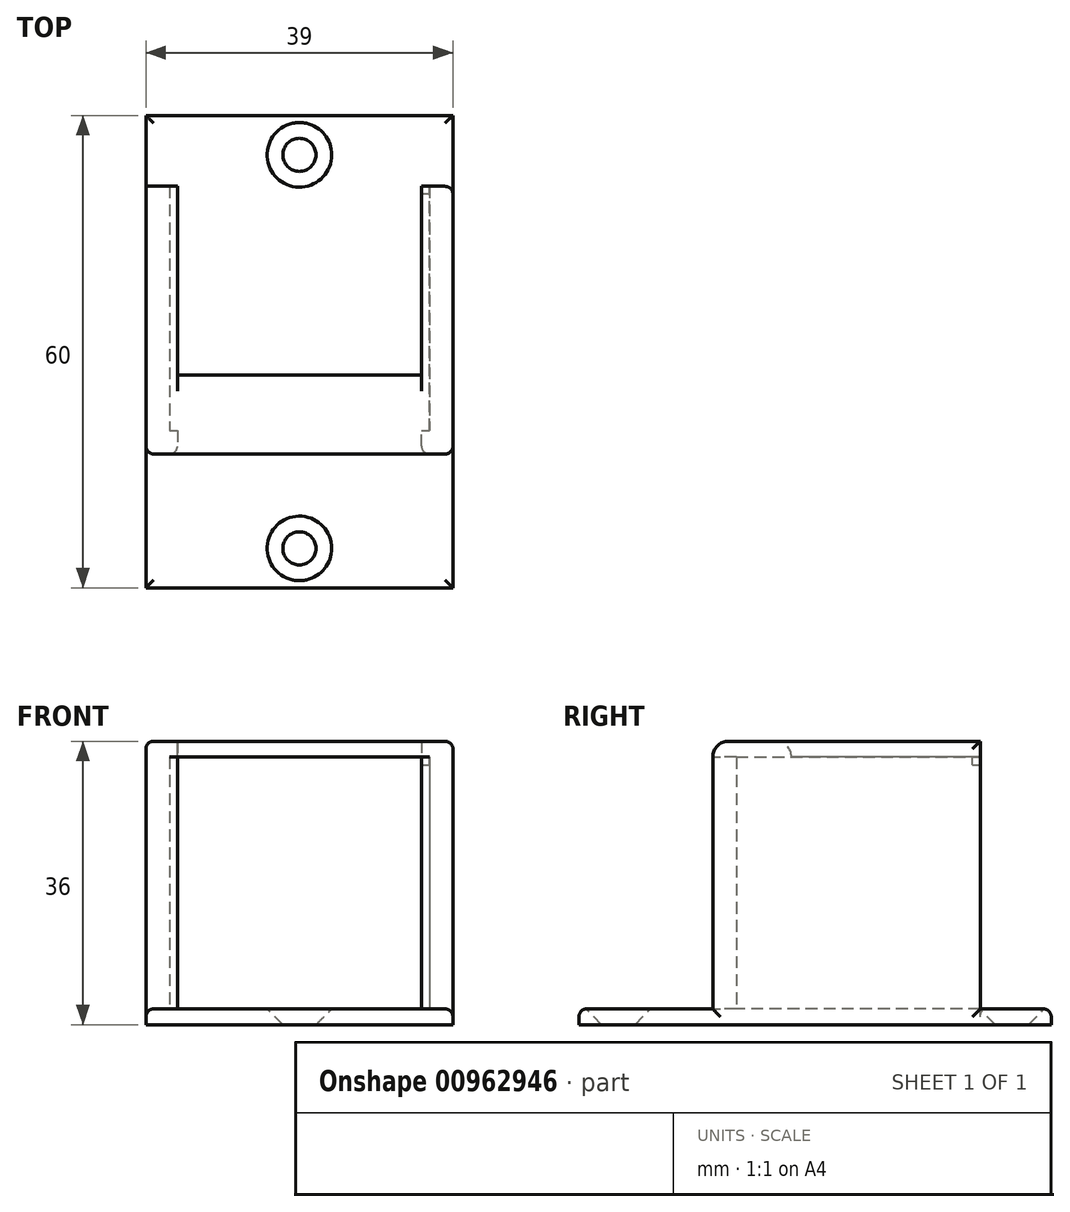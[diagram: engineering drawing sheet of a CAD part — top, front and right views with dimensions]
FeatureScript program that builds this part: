
annotation { "Feature Type Name" : "Feature", "Feature Type Description" : "" }
export const myFeature = defineFeature(function(context is Context, id is Id, definition is map)
    precondition{}
    {
        {
            var Q0;
            Q0=qCreatedBy(makeId("Top.planeOp"),FACE);
            var sketch = newSketch(context, id + "F0", { "sketchPlane" : qUnion([Q0])});
            skLineSegment(sketch, "E0.bottom", {"start": v(19.5, 25) * mm, "end": v(16.5, 25) * mm});
            skLineSegment(sketch, "E0.top", {"start": v(19.5, -25) * mm, "end": v(-19.5, -25) * mm});
            skLineSegment(sketch, "E0.left", {"start": v(19.5, 25) * mm, "end": v(19.5, -25) * mm});
            skLineSegment(sketch, "E0.right", {"start": v(-19.5, 25) * mm, "end": v(-19.5, -25) * mm});
            skPoint(sketch, "E1.middle", {"position": v(0, 0) * mm});
            skLineSegment(sketch, "E2", {"start": v(0, -25) * mm, "end": v(0, -20) * mm, "construction": true});
            skCircle(sketch, "E3", {"center": v(0, -20) * mm, "radius": 2.1 * mm});
            skLineSegment(sketch, "E4.bottom", {"start": v(-16.5, 15) * mm, "end": v(16.5, 15) * mm});
            skLineSegment(sketch, "E4.top", {"start": v(-16.5, -15) * mm, "end": v(16.5, -15) * mm});
            skLineSegment(sketch, "E4.left", {"start": v(-16.5, 15) * mm, "end": v(-16.5, -15) * mm});
            skLineSegment(sketch, "E4.right", {"start": v(16.5, 15) * mm, "end": v(16.5, -15) * mm});
            skLineSegment(sketch, "E5", {"start": v(-16.5, 15) * mm, "end": v(-16.5, 25) * mm});
            skLineSegment(sketch, "E6", {"start": v(-16.5, 25) * mm, "end": v(-16.5, -25) * mm});
            skLineSegment(sketch, "E7", {"start": v(16.5, -25) * mm, "end": v(16.5, 25) * mm});
            skLineSegment(sketch, "E8", {"start": v(-16.5, -15) * mm, "end": v(-19.5, -15) * mm});
            skLineSegment(sketch, "E9", {"start": v(16.5, -15) * mm, "end": v(19.5, -15) * mm});
            skLineSegment(sketch, "E10", {"start": v(16.5, -15) * mm, "end": v(15.5, -15) * mm});
            skLineSegment(sketch, "E11", {"start": v(16.5, -15) * mm, "end": v(16.5, -18) * mm, "construction": true});
            skLineSegment(sketch, "E12", {"start": v(16.5, -18) * mm, "end": v(19.5, -18) * mm});
            skLineSegment(sketch, "E13", {"start": v(-16.5, -18) * mm, "end": v(-19.5, -18) * mm});
            skLineSegment(sketch, "E14", {"start": v(-16.5, -15) * mm, "end": v(-15.5, -15) * mm});
            skLineSegment(sketch, "E15", {"start": v(-15.5, -15) * mm, "end": v(-15.5, -18) * mm});
            skLineSegment(sketch, "E16", {"start": v(-15.5, -18) * mm, "end": v(-16.5, -18) * mm});
            skLineSegment(sketch, "E17", {"start": v(16.5, -18) * mm, "end": v(15.5, -18) * mm});
            skLineSegment(sketch, "E18", {"start": v(15.5, -18) * mm, "end": v(15.5, -15) * mm});
            skLineSegment(sketch, "E19", {"start": v(-19.5, 15) * mm, "end": v(-19.5, 16) * mm});
            skLineSegment(sketch, "E20", {"start": v(-19.5, 16) * mm, "end": v(-16.5, 16) * mm});
            skLineSegment(sketch, "E21", {"start": v(-16.5, 16) * mm, "end": v(-16.5, 15) * mm});
            skLineSegment(sketch, "E22", {"start": v(16.5, 15) * mm, "end": v(16.5, 16) * mm});
            skLineSegment(sketch, "E23", {"start": v(16.5, 16) * mm, "end": v(19.5, 16) * mm});
            skLineSegment(sketch, "E24.trimOffspring", {"start": v(-16.5, 25) * mm, "end": v(-19.5, 25) * mm});
            skPoint(sketch, "E25.startSnap0", {"position": v(-18, 25) * mm});
            skLineSegment(sketch, "E26", {"start": v(-19.5, 25) * mm, "end": v(19.5, 25) * mm});
            skLineSegment(sketch, "E27", {"start": v(0, 25) * mm, "end": v(0, 20) * mm, "construction": true});
            skCircle(sketch, "E28", {"center": v(0, 20) * mm, "radius": 2.1 * mm});
            skLineSegment(sketch, "E29", {"start": v(19.5, -25) * mm, "end": v(19.5, -35) * mm});
            skLineSegment(sketch, "E30", {"start": v(19.5, -35) * mm, "end": v(-19.5, -35) * mm});
            skLineSegment(sketch, "E31", {"start": v(-19.5, -35) * mm, "end": v(-19.5, -25) * mm});
            skLineSegment(sketch, "E32", {"start": v(0, -35) * mm, "end": v(0, -30) * mm, "construction": true});
            skCircle(sketch, "E33", {"center": v(0, -30) * mm, "radius": 2.1 * mm});
            skSolve(sketch);
        }
        {
            var Q0;
            {var subQ1=sQuery(id+"F0.wireOp",EDGE,"E4.left");var subQ2=sQuery(id+"F0.wireOp",EDGE,"E4.bottom");var subQ3=sQuery(id+"F0.wireOp",EDGE,"E20");var subQ10=sQuery(id+"F0.wireOp",EDGE,"E0.bottom");var subQ14=sQuery(id+"F0.wireOp",EDGE,"E4.right");var subQ19=sQuery(id+"F0.wireOp",EDGE,"E8");var subQ21=makeQuery(id+"F0.imprint","IMPRINT",EDGE,{"derivedFrom":subQ19});var subQ22=makeQuery(id+"F0.imprint","IMPRINT",EDGE,{"derivedFrom":subQ3});var subQ23=sQuery(id+"F0.wireOp",EDGE,"E9");var subQ24=makeQuery(id+"F0.imprint","IMPRINT",EDGE,{"derivedFrom":subQ23});var subQ36=sQuery(id+"F0.wireOp",EDGE,"E29");var subQ39=sQuery(id+"F0.wireOp",EDGE,"E13");var subQ41=makeQuery(id+"F0.imprint","IMPRINT",EDGE,{"derivedFrom":subQ39});var subQ44=sQuery(id+"F0.wireOp",EDGE,"E12");var subQ47=makeQuery(id+"F0.imprint","IMPRINT",EDGE,{"derivedFrom":subQ44});Q0=qUnion([makeQuery(id+"F0.imprint","IMPRINT",FACE,{"disambiguationData":[TD([[makeQuery(id+"F0.imprint","IMPRINT",EDGE,{"derivedFrom":subQ10}),1.0]])]}),makeQuery(id+"F0.imprint","IMPRINT",FACE,{"disambiguationData":[TD([[subQ22,1.0]])]}),makeQuery(id+"F0.imprint","IMPRINT",FACE,{"disambiguationData":[TD([[subQ47,-1.0]])]}),makeQuery(id+"F0.imprint","IMPRINT",FACE,{"disambiguationData":[TD([[subQ41,1.0]])]}),makeQuery(id+"F0.imprint","IMPRINT",FACE,{"disambiguationData":[TD([[subQ24,-1.0]])]}),makeQuery(id+"F0.imprint","IMPRINT",FACE,{"disambiguationData":[TD([[subQ21,1.0]])]}),makeQuery(id+"F0.imprint","IMPRINT",FACE,{"disambiguationData":[TD([[makeQuery(id+"F0.imprint","IMPRINT",EDGE,{"derivedFrom":subQ36}),-1.0]])]}),makeQuery(id+"F0.imprint","IMPRINT",FACE,{"disambiguationData":[TD([[makeQuery(id+"F0.imprint","IMPRINT",EDGE,{"derivedFrom":subQ14}),1.0]])]}),makeQuery(id+"F0.imprint","IMPRINT",FACE,{"disambiguationData":[TD([[makeQuery(id+"F0.imprint","IMPRINT",EDGE,{"derivedFrom":subQ1}),-1.0]])]}),makeQuery(id+"F0.imprint","IMPRINT",FACE,{"disambiguationData":[TD([[makeQuery(id+"F0.imprint","IMPRINT",EDGE,{"derivedFrom":subQ2}),1.0]])]})]);}
            var Q1;
            Q1=makeQuery(id+"F0.imprint","IMPRINT",FACE,{"disambiguationData":[TD([[makeQuery(id+"F0.imprint","IMPRINT",EDGE,{"derivedFrom":sQuery(id+"F0.wireOp",EDGE,"E4.bottom")}),-1.0]])]});
            var Q2;
            {var subQ0=sQuery(id+"F0.wireOp",EDGE,"E15");Q2=makeQuery(id+"F0.imprint","IMPRINT",FACE,{"disambiguationData":[TD([[makeQuery(id+"F0.imprint","IMPRINT",EDGE,{"derivedFrom":subQ0}),-1.0]])]});}
            var Q3;
            {var subQ4=sQuery(id+"F0.wireOp",EDGE,"E17");Q3=makeQuery(id+"F0.imprint","IMPRINT",FACE,{"disambiguationData":[TD([[makeQuery(id+"F0.imprint","IMPRINT",EDGE,{"derivedFrom":subQ4}),-1.0]])]});}
            var Q4;
            Q4=makeQuery(id+"F0.imprint","IMPRINT",FACE,{"disambiguationData":[TD([[makeQuery(id+"F0.imprint","IMPRINT",EDGE,{"derivedFrom":sQuery(id+"F0.wireOp",EDGE,"E3")}),-1.0]])]});
            var Q5;
            Q5=makeQuery(id+"F0.imprint","IMPRINT",FACE,{"disambiguationData":[TD([[makeQuery(id+"F0.imprint","IMPRINT",EDGE,{"derivedFrom":sQuery(id+"F0.wireOp",EDGE,"E3")}),1.0]])]});
            extrude(context, id + "F1", {"entities" : qUnion([Q0, Q1, Q2, Q3, Q4, Q5]), "oppositeDirection" : true, "depth" : 2 * mm, "offsetDistance" : 25 * mm});
        }
        {
            var Q0;
            {var subQ1=sQuery(id+"F0.wireOp",EDGE,"E4.left");Q0=makeQuery(id+"F0.imprint","IMPRINT",FACE,{"disambiguationData":[TD([[makeQuery(id+"F0.imprint","IMPRINT",EDGE,{"derivedFrom":subQ1}),-1.0]])]});}
            var Q1;
            {var subQ0=sQuery(id+"F0.wireOp",EDGE,"E8");Q1=makeQuery(id+"F0.imprint","IMPRINT",FACE,{"disambiguationData":[TD([[makeQuery(id+"F0.imprint","IMPRINT",EDGE,{"derivedFrom":subQ0}),1.0]])]});}
            var Q2;
            {var subQ0=sQuery(id+"F0.wireOp",EDGE,"nsobvpxD-CgMy-OlzF-O2xX-1xosLkDLj3p1");Q2=makeQuery(id+"F0.imprint","IMPRINT",FACE,{"disambiguationData":[TD([[makeQuery(id+"F0.imprint","IMPRINT",EDGE,{"derivedFrom":subQ0}),-1.0]])]});}
            var Q3;
            {var subQ2=sQuery(id+"F0.wireOp",EDGE,"E9");Q3=makeQuery(id+"F0.imprint","IMPRINT",FACE,{"disambiguationData":[TD([[makeQuery(id+"F0.imprint","IMPRINT",EDGE,{"derivedFrom":subQ2}),-1.0]])]});}
            var Q4;
            {var subQ4=sQuery(id+"F0.wireOp",EDGE,"E17");Q4=makeQuery(id+"F0.imprint","IMPRINT",FACE,{"disambiguationData":[TD([[makeQuery(id+"F0.imprint","IMPRINT",EDGE,{"derivedFrom":subQ4}),-1.0]])]});}
            var Q5;
            {var subQ0=sQuery(id+"F0.wireOp",EDGE,"E15");Q5=makeQuery(id+"F0.imprint","IMPRINT",FACE,{"disambiguationData":[TD([[makeQuery(id+"F0.imprint","IMPRINT",EDGE,{"derivedFrom":subQ0}),-1.0]])]});}
            var Q6;
            {var subQ1=sQuery(id+"F0.wireOp",EDGE,"E4.right");Q6=makeQuery(id+"F0.imprint","IMPRINT",FACE,{"disambiguationData":[TD([[makeQuery(id+"F0.imprint","IMPRINT",EDGE,{"derivedFrom":subQ1}),1.0]])]});}
            extrude(context, id + "F2", {"entities" : qUnion([Q0, Q1, Q2, Q3, Q4, Q5, Q6]), "operationType" : NewBodyOperationType.ADD, "depth" : 34 * mm, "offsetDistance" : 25 * mm});
        }
        {
            var Q0;
            Q0=makeQuery(id+"F2.opExtrude","SWEPT_FACE",FACE,{"disambiguationData":[OSD([sQuery(id+"F0.wireOp",EDGE,"E12"),sQuery(id+"F0.wireOp",EDGE,"E17")])]});
            var sketch = newSketch(context, id + "F3", { "sketchPlane" : qUnion([Q0])});
            skLineSegment(sketch, "E34", {"start": v(-19.5, 0) * mm, "end": v(-19.5, 34) * mm, "construction": true});
            skLineSegment(sketch, "E35", {"start": v(-19.5, 34) * mm, "end": v(-15.5, 34) * mm, "construction": true});
            skLineSegment(sketch, "E36", {"start": v(-19.5, 34) * mm, "end": v(-19.5, 32) * mm});
            skLineSegment(sketch, "E37", {"start": v(-19.5, 34) * mm, "end": v(-15.5, 34) * mm});
            skLineSegment(sketch, "E38", {"start": v(-15.5, 34) * mm, "end": v(-15.5, 30.98) * mm});
            skLineSegment(sketch, "E39", {"start": v(19.5, 34) * mm, "end": v(15.5, 34) * mm});
            skLineSegment(sketch, "E40", {"start": v(15.5, 34) * mm, "end": v(15.5, 32) * mm});
            skLineSegment(sketch, "E41", {"start": v(15.5, 32) * mm, "end": v(19.5, 32) * mm});
            skLineSegment(sketch, "E42", {"start": v(-19.5, 32) * mm, "end": v(-15.5, 32) * mm});
            skLineSegment(sketch, "E43", {"start": v(15.5, 32) * mm, "end": v(-15.5, 32) * mm});
            skLineSegment(sketch, "E44", {"start": v(-15.5, 34) * mm, "end": v(15.5, 34) * mm});
            skSolve(sketch);
        }
        {
            var Q0;
            Q0=makeQuery(id+"F3.imprint","IMPRINT",FACE,{"disambiguationData":[TD([[makeQuery(id+"F3.imprint","IMPRINT",EDGE,{"derivedFrom":sQuery(id+"F3.wireOp",EDGE,"E36")}),1.0]])]});
            var Q1;
            {var subQ0=sQuery(id+"F3.wireOp",EDGE,"E39");Q1=makeQuery(id+"F3.imprint","IMPRINT",FACE,{"disambiguationData":[TD([[makeQuery(id+"F3.imprint","IMPRINT",EDGE,{"derivedFrom":subQ0}),-1.0]])]});}
            extrude(context, id + "F4", {"entities" : qUnion([Q0, Q1]), "operationType" : NewBodyOperationType.ADD, "oppositeDirection" : true, "depth" : 34 * mm, "offsetDistance" : 25 * mm});
        }
        {
            var Q0;
            Q0=makeQuery(id+"F1.opExtrude","CAP_EDGE",EDGE,{"disambiguationData":[OSD([sQuery(id+"F0.wireOp",EDGE,"E33")])],"isStart":true});
            var Q1;
            Q1=makeQuery(id+"F1.opExtrude","CAP_EDGE",EDGE,{"disambiguationData":[OSD([sQuery(id+"F0.wireOp",EDGE,"E28")])],"isStart":true});
            chamfer(context, id + "F5", {"entities" : qUnion([Q0, Q1]), "width" : 2 * mm, "tangentPropagation" : true});
        }
        {
            var Q0;
            Q0=makeQuery(id+"F1.opExtrude","CAP_EDGE",EDGE,{"disambiguationData":[OSD([sQuery(id+"F0.wireOp",EDGE,"E0.bottom")])],"isStart":true});
            var Q1;
            {var subQ0=sQuery(id+"F0.wireOp",EDGE,"E0.right");var subQ1=sQuery(id+"F0.wireOp",EDGE,"E0.bottom");Q1=makeQuery(id+"F2.boolean.opBoolean","SPLIT",EDGE,{"disambiguationData":[TD([makeQuery(id+"F1.opExtrude","SWEPT_FACE",FACE,{"disambiguationData":[OSD([subQ1])]})])],"derivedFrom":makeQuery(id+"F1.opExtrude","CAP_EDGE",EDGE,{"disambiguationData":[OSD([subQ0])],"isStart":true})});}
            var Q2;
            {var subQ0=sQuery(id+"F0.wireOp",EDGE,"E0.right");var subQ1=sQuery(id+"F0.wireOp",EDGE,"E0.top");Q2=makeQuery(id+"F2.boolean.opBoolean","SPLIT",EDGE,{"disambiguationData":[TD([makeQuery(id+"F1.opExtrude","SWEPT_FACE",FACE,{"disambiguationData":[OSD([subQ1])]})])],"derivedFrom":makeQuery(id+"F1.opExtrude","CAP_EDGE",EDGE,{"disambiguationData":[OSD([subQ0])],"isStart":true})});}
            var Q3;
            Q3=makeQuery(id+"F1.opExtrude","CAP_EDGE",EDGE,{"disambiguationData":[OSD([sQuery(id+"F0.wireOp",EDGE,"E0.top")])],"isStart":true});
            var Q4;
            {var subQ0=sQuery(id+"F0.wireOp",EDGE,"E0.left");var subQ1=sQuery(id+"F0.wireOp",EDGE,"E0.top");Q4=makeQuery(id+"F2.boolean.opBoolean","SPLIT",EDGE,{"disambiguationData":[TD([makeQuery(id+"F1.opExtrude","SWEPT_FACE",FACE,{"disambiguationData":[OSD([subQ1])]})])],"derivedFrom":makeQuery(id+"F1.opExtrude","CAP_EDGE",EDGE,{"disambiguationData":[OSD([subQ0])],"isStart":true})});}
            var Q5;
            {var subQ0=sQuery(id+"F0.wireOp",EDGE,"E0.left");var subQ1=sQuery(id+"F0.wireOp",EDGE,"E0.bottom");Q5=makeQuery(id+"F2.boolean.opBoolean","SPLIT",EDGE,{"disambiguationData":[TD([makeQuery(id+"F1.opExtrude","SWEPT_FACE",FACE,{"disambiguationData":[OSD([subQ1])]})])],"derivedFrom":makeQuery(id+"F1.opExtrude","CAP_EDGE",EDGE,{"disambiguationData":[OSD([subQ0])],"isStart":true})});}
            var Q6;
            Q6=makeQuery(id+"F2.opExtrude","SWEPT_EDGE",EDGE,{"disambiguationData":[OSD([sQuery(id+"F0.wireOp",EDGE,"E0.right"),sQuery(id+"F0.wireOp",EDGE,"E13")])]});
            var Q7;
            Q7=makeQuery(id+"F2.opExtrude","CAP_EDGE",EDGE,{"disambiguationData":[OSD([sQuery(id+"F0.wireOp",EDGE,"E0.right")])],"isStart":false});
            var Q8;
            {var subQ0=sQuery(id+"F0.wireOp",EDGE,"E0.left");Q8=qUnion([makeQuery(id+"F2.opExtrude","SWEPT_EDGE",EDGE,{"disambiguationData":[OSD([subQ0,sQuery(id+"F0.wireOp",EDGE,"E12")])]}),makeQuery(id+"F2.opExtrude","SWEPT_EDGE",EDGE,{"disambiguationData":[OSD([subQ0,sQuery(id+"F0.wireOp",EDGE,"E23")])]})]);}
            var Q9;
            Q9=makeQuery(id+"F2.opExtrude","CAP_EDGE",EDGE,{"disambiguationData":[OSD([sQuery(id+"F0.wireOp",EDGE,"E0.left")])],"isStart":false});
            var Q10;
            Q10=makeQuery(id+"F2.opExtrude","SWEPT_EDGE",EDGE,{"disambiguationData":[OSD([sQuery(id+"F0.wireOp",EDGE,"E0.right"),sQuery(id+"F0.wireOp",EDGE,"E13")])]});
            var Q11;
            Q11=makeQuery(id+"F2.opExtrude","SWEPT_EDGE",EDGE,{"disambiguationData":[OSD([sQuery(id+"F0.wireOp",EDGE,"E0.left"),sQuery(id+"F0.wireOp",EDGE,"E12")])]});
            var Q12;
            {var subQ0=sQuery(id+"F0.wireOp",EDGE,"E0.left");var subQ1=sQuery(id+"F0.wireOp",EDGE,"E30");var subQ2=sQuery(id+"F0.wireOp",EDGE,"E29");Q12=makeQuery(id+"F2.boolean.opBoolean","SPLIT",EDGE,{"disambiguationData":[TD([makeQuery(id+"F1.opExtrude","SWEPT_FACE",FACE,{"disambiguationData":[OSD([subQ1])]})])],"derivedFrom":makeQuery(id+"F1.opExtrude","CAP_EDGE",EDGE,{"disambiguationData":[OSD([subQ0,subQ2])],"isStart":true})});}
            var Q13;
            Q13=makeQuery(id+"F1.opExtrude","CAP_EDGE",EDGE,{"disambiguationData":[OSD([sQuery(id+"F0.wireOp",EDGE,"E30")])],"isStart":true});
            var Q14;
            {var subQ0=sQuery(id+"F0.wireOp",EDGE,"E30");var subQ1=sQuery(id+"F0.wireOp",EDGE,"E0.right");var subQ2=sQuery(id+"F0.wireOp",EDGE,"E31");Q14=makeQuery(id+"F2.boolean.opBoolean","SPLIT",EDGE,{"disambiguationData":[TD([makeQuery(id+"F1.opExtrude","SWEPT_FACE",FACE,{"disambiguationData":[OSD([subQ0])]})])],"derivedFrom":makeQuery(id+"F1.opExtrude","CAP_EDGE",EDGE,{"disambiguationData":[OSD([subQ1,subQ2])],"isStart":true})});}
            var Q15;
            {var subQ0=sQuery(id+"F0.wireOp",EDGE,"E0.left");var subQ1=sQuery(id+"F0.wireOp",EDGE,"E29");Q15=makeQuery(id+"F2.boolean.opBoolean","SPLIT",EDGE,{"disambiguationData":[TD([makeQuery(id+"F2.opExtrude","SWEPT_FACE",FACE,{"disambiguationData":[OSD([sQuery(id+"F0.wireOp",EDGE,"E23")])]})])],"derivedFrom":makeQuery(id+"F1.opExtrude","CAP_EDGE",EDGE,{"disambiguationData":[OSD([subQ0,subQ1])],"isStart":true})});}
            var Q16;
            Q16=makeQuery(id+"F1.opExtrude","CAP_EDGE",EDGE,{"disambiguationData":[OSD([sQuery(id+"F0.wireOp",EDGE,"E0.bottom"),sQuery(id+"F0.wireOp",EDGE,"E24.trimOffspring"),sQuery(id+"F0.wireOp",EDGE,"E26")])],"isStart":true});
            var Q17;
            {var subQ0=sQuery(id+"F0.wireOp",EDGE,"E0.right");var subQ1=sQuery(id+"F0.wireOp",EDGE,"E31");Q17=makeQuery(id+"F2.boolean.opBoolean","SPLIT",EDGE,{"disambiguationData":[TD([makeQuery(id+"F2.opExtrude","SWEPT_FACE",FACE,{"disambiguationData":[OSD([sQuery(id+"F0.wireOp",EDGE,"E20")])]})])],"derivedFrom":makeQuery(id+"F1.opExtrude","CAP_EDGE",EDGE,{"disambiguationData":[OSD([subQ0,subQ1])],"isStart":true})});}
            fillet(context, id + "F6", {"entities" : qUnion([Q0, Q1, Q2, Q3, Q4, Q5, Q6, Q7, Q8, Q9, Q10, Q11, Q12, Q13, Q14, Q15, Q16, Q17]), "radius" : 1 * mm, "tangentPropagation" : true, "allowEdgeOverflow" : false});
        }
        {
            var Q0;
            Q0=makeQuery(id+"F4.boolean.opBoolean","MERGE",FACE,{"derivedFrom":[makeQuery(id+"F2.opExtrude","SWEPT_FACE",FACE,{"disambiguationData":[OSD([sQuery(id+"F0.wireOp",EDGE,"E20")])]}),makeQuery(id+"F4.opExtrude","CAP_FACE",FACE,{"disambiguationData":[OSD([sQuery(id+"F3.wireOp",EDGE,"E36"),sQuery(id+"F3.wireOp",EDGE,"E37"),sQuery(id+"F3.wireOp",EDGE,"E38"),sQuery(id+"F3.wireOp",EDGE,"E42")])],"isStart":false})]});
            var sketch = newSketch(context, id + "F7", { "sketchPlane" : qUnion([Q0])});
            skLineSegment(sketch, "E45", {"start": v(-15.5, 32) * mm, "end": v(-15.5, 31) * mm});
            skLineSegment(sketch, "E46", {"start": v(-15.5, 31) * mm, "end": v(-16.5, 31) * mm});
            skLineSegment(sketch, "E47", {"start": v(-16.5, 31) * mm, "end": v(-16.5, 32) * mm});
            skLineSegment(sketch, "E48", {"start": v(-16.5, 32) * mm, "end": v(-15.5, 32) * mm});
            skLineSegment(sketch, "E49", {"start": v(15.5, 34) * mm, "end": v(15.5, 33) * mm});
            skLineSegment(sketch, "E50", {"start": v(15.5, 33) * mm, "end": v(16.5, 33) * mm});
            skLineSegment(sketch, "E51", {"start": v(16.5, 32) * mm, "end": v(16.5, 33) * mm});
            skLineSegment(sketch, "E52", {"start": v(16.5, 32) * mm, "end": v(15.5, 34) * mm});
            skSolve(sketch);
        }
        {
            var Q0;
            Q0=makeQuery(id+"F7.imprint","IMPRINT",FACE,{"disambiguationData":[TD([[makeQuery(id+"F7.imprint","IMPRINT",EDGE,{"derivedFrom":sQuery(id+"F7.wireOp",EDGE,"E45")}),-1.0]])]});
            var Q1;
            Q1=makeQuery(id+"F7.imprint","IMPRINT",FACE,{"disambiguationData":[TD([[makeQuery(id+"F7.imprint","IMPRINT",EDGE,{"derivedFrom":sQuery(id+"F7.wireOp",EDGE,"E49")}),1.0]])]});
            extrude(context, id + "F8", {"entities" : qUnion([Q0, Q1]), "operationType" : NewBodyOperationType.ADD, "oppositeDirection" : true, "depth" : 1 * mm, "offsetDistance" : 25 * mm});
        }
        {
            var Q0;
            Q0=makeQuery(id+"F3.imprint","IMPRINT",FACE,{"disambiguationData":[TD([[makeQuery(id+"F3.imprint","IMPRINT",EDGE,{"derivedFrom":sQuery(id+"F3.wireOp",EDGE,"E40")}),-1.0]])]});
            extrude(context, id + "F9", {"entities" : qUnion([Q0]), "operationType" : NewBodyOperationType.ADD, "oppositeDirection" : true, "depth" : 10 * mm, "offsetDistance" : 25 * mm});
        }
        {
            var Q0;
            Q0=makeQuery(id+"F9.boolean.opBoolean","MERGE",EDGE,{"derivedFrom":[makeQuery(id+"F2.opExtrude","CAP_EDGE",EDGE,{"disambiguationData":[OSD([sQuery(id+"F0.wireOp",EDGE,"E12"),sQuery(id+"F0.wireOp",EDGE,"E17")])],"isStart":false}),makeQuery(id+"F2.opExtrude","CAP_EDGE",EDGE,{"disambiguationData":[OSD([sQuery(id+"F0.wireOp",EDGE,"E13"),sQuery(id+"F0.wireOp",EDGE,"E16")])],"isStart":false}),makeQuery(id+"F9.opExtrude","CAP_EDGE",EDGE,{"disambiguationData":[OSD([sQuery(id+"F3.wireOp",EDGE,"E44")])],"isStart":true})]});
            var Q1;
            Q1=makeQuery(id+"F4.boolean.opBoolean","MERGE",EDGE,{"derivedFrom":[makeQuery(id+"F2.opExtrude","CAP_EDGE",EDGE,{"disambiguationData":[OSD([sQuery(id+"F0.wireOp",EDGE,"E15")])],"isStart":false}),makeQuery(id+"F4.opExtrude","SWEPT_EDGE",EDGE,{"disambiguationData":[OSD([sQuery(id+"F3.wireOp",EDGE,"E37"),sQuery(id+"F3.wireOp",EDGE,"E38"),sQuery(id+"F3.wireOp",EDGE,"E44")])]})]});
            var Q2;
            Q2=makeQuery(id+"F9.opExtrude","CAP_EDGE",EDGE,{"disambiguationData":[OSD([sQuery(id+"F3.wireOp",EDGE,"E44")])],"isStart":false});
            var Q3;
            Q3=makeQuery(id+"F4.boolean.opBoolean","MERGE",EDGE,{"derivedFrom":[makeQuery(id+"F2.opExtrude","CAP_EDGE",EDGE,{"disambiguationData":[OSD([sQuery(id+"F0.wireOp",EDGE,"E18")])],"isStart":false}),makeQuery(id+"F4.opExtrude","SWEPT_EDGE",EDGE,{"disambiguationData":[OSD([sQuery(id+"F3.wireOp",EDGE,"E39"),sQuery(id+"F3.wireOp",EDGE,"E40"),sQuery(id+"F3.wireOp",EDGE,"E44")])]})]});
            fillet(context, id + "F10", {"entities" : qUnion([Q0, Q1, Q2, Q3]), "radius" : 2 * mm, "tangentPropagation" : true, "allowEdgeOverflow" : false});
        }
        {
            var Q0;
            Q0=makeQuery(id+"F2.opExtrude","SWEPT_EDGE",EDGE,{"disambiguationData":[OSD([sQuery(id+"F0.wireOp",EDGE,"E15"),sQuery(id+"F0.wireOp",EDGE,"E16")])]});
            var Q1;
            Q1=makeQuery(id+"F2.opExtrude","SWEPT_EDGE",EDGE,{"disambiguationData":[OSD([sQuery(id+"F0.wireOp",EDGE,"E17"),sQuery(id+"F0.wireOp",EDGE,"E18")])]});
            fillet(context, id + "F11", {"entities" : qUnion([Q0, Q1]), "radius" : 1 * mm, "tangentPropagation" : true, "allowEdgeOverflow" : false});
        }
    });
